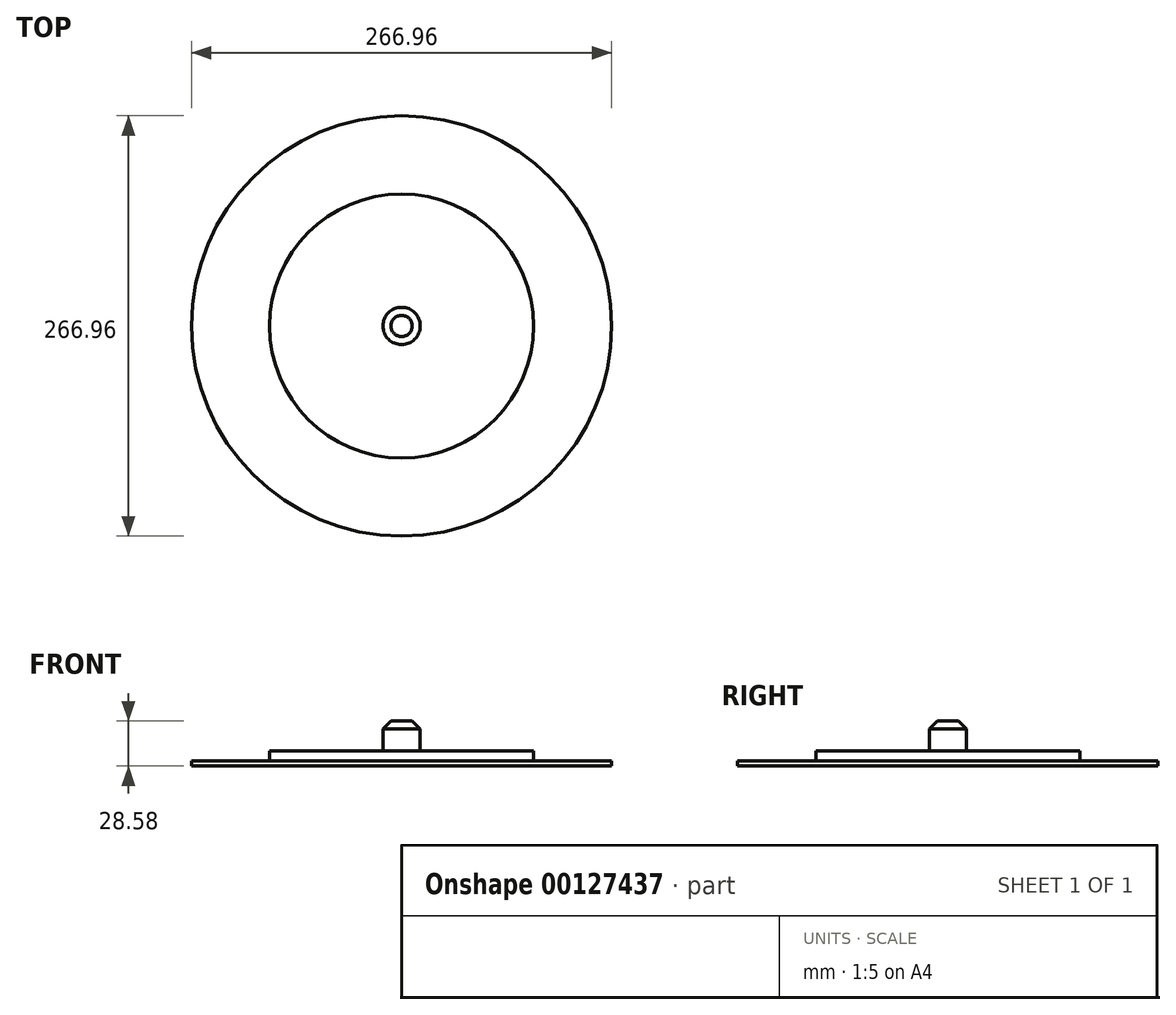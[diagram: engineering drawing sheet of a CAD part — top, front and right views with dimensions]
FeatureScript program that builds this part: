
annotation { "Feature Type Name" : "Feature", "Feature Type Description" : "" }
export const myFeature = defineFeature(function(context is Context, id is Id, definition is map)
    precondition{}
    {
        {
            var Q0;
            Q0=qCreatedBy(makeId("Top.planeOp"),FACE);
            var sketch = newSketch(context, id + "F0", { "sketchPlane" : qUnion([Q0])});
            skCircle(sketch, "E0", {"center": v(0, 0) * mm, "radius": 75.67 * mm});
            skCircle(sketch, "E1", {"center": v(0, 0) * mm, "radius": 56.5 * mm});
            skCircle(sketch, "E2", {"center": v(0, 0) * mm, "radius": 10.67 * mm});
            skSolve(sketch);
        }
        {
            var Q0;
            Q0=makeQuery(id+"F0.imprint","IMPRINT",FACE,{"disambiguationData":[TD([[makeQuery(id+"F0.imprint","IMPRINT",EDGE,{"derivedFrom":sQuery(id+"F0.wireOp",EDGE,"E2")}),1.0]])]});
            var Q1;
            Q1=makeQuery(id+"F0.imprint","IMPRINT",FACE,{"disambiguationData":[TD([[makeQuery(id+"F0.imprint","IMPRINT",EDGE,{"derivedFrom":sQuery(id+"F0.wireOp",EDGE,"E1")}),1.0]])]});
            extrude(context, id + "F1", {"entities" : qUnion([Q0, Q1]), "depth" : 3.17 * mm});
        }
        {
            var Q0;
            Q0=makeQuery(id+"F1.opExtrude","CAP_FACE",FACE,{"disambiguationData":[OSD([sQuery(id+"F0.wireOp",EDGE,"E1")])],"isStart":false});
            var sketch = newSketch(context, id + "F2", { "sketchPlane" : qUnion([Q0])});
            skCircle(sketch, "E3", {"center": v(0, 0) * mm, "radius": 83.84 * mm});
            skSolve(sketch);
        }
        {
            var Q0;
            Q0=makeQuery(id+"F2.imprint","IMPRINT",FACE,{"disambiguationData":[TD([[makeQuery(id+"F2.imprint","IMPRINT",EDGE,{"derivedFrom":makeQuery(id+"F1.opExtrude","CAP_EDGE",EDGE,{"disambiguationData":[OSD([sQuery(id+"F0.wireOp",EDGE,"E1")])],"isStart":false})}),1.0]])]});
            var sketch = newSketch(context, id + "F3", { "sketchPlane" : qUnion([Q0])});
            skCircle(sketch, "E4", {"center": v(0, 0) * mm, "radius": 11.84 * mm});
            skSolve(sketch);
        }
        {
            var Q0;
            Q0=makeQuery(id+"F3.imprint","IMPRINT",FACE,{"disambiguationData":[TD([[makeQuery(id+"F3.imprint","IMPRINT",EDGE,{"derivedFrom":sQuery(id+"F3.wireOp",EDGE,"E4")}),1.0]])]});
            extrude(context, id + "F4", {"entities" : qUnion([Q0]), "operationType" : NewBodyOperationType.ADD, "depth" : 25.4 * mm});
        }
        {
            var Q0;
            Q0=makeQuery(id+"F2.imprint","IMPRINT",FACE,{"disambiguationData":[TD([[makeQuery(id+"F2.imprint","IMPRINT",EDGE,{"derivedFrom":makeQuery(id+"F1.opExtrude","CAP_EDGE",EDGE,{"disambiguationData":[OSD([sQuery(id+"F0.wireOp",EDGE,"E1")])],"isStart":false})}),1.0]])]});
            var Q1;
            Q1=makeQuery(id+"F2.imprint","IMPRINT",FACE,{"disambiguationData":[TD([[makeQuery(id+"F2.imprint","IMPRINT",EDGE,{"derivedFrom":sQuery(id+"F2.wireOp",EDGE,"E3")}),1.0]])]});
            extrude(context, id + "F5", {"entities" : qUnion([Q0, Q1]), "operationType" : NewBodyOperationType.ADD, "depth" : 6.35 * mm});
        }
        {
            var Q0;
            Q0=makeQuery(id+"F4.opExtrude","CAP_EDGE",EDGE,{"disambiguationData":[OSD([sQuery(id+"F3.wireOp",EDGE,"E4")])],"isStart":false});
            chamfer(context, id + "F6", {"entities" : qUnion([Q0]), "width" : 5.08 * mm, "tangentPropagation" : true});
        }
        {
            var Q0;
            Q0=qCreatedBy(makeId("Top.planeOp"),FACE);
            var sketch = newSketch(context, id + "F7", { "sketchPlane" : qUnion([Q0])});
            skCircle(sketch, "E5", {"center": v(0, 0) * mm, "radius": 133.48 * mm});
            skSolve(sketch);
        }
        {
            var Q0;
            Q0 = qSketchRegion(id + "F7", true);
            extrude(context, id + "F8", {"entities" : qUnion([Q0]), "operationType" : NewBodyOperationType.ADD, "depth" : 3.17 * mm});
        }
    });
